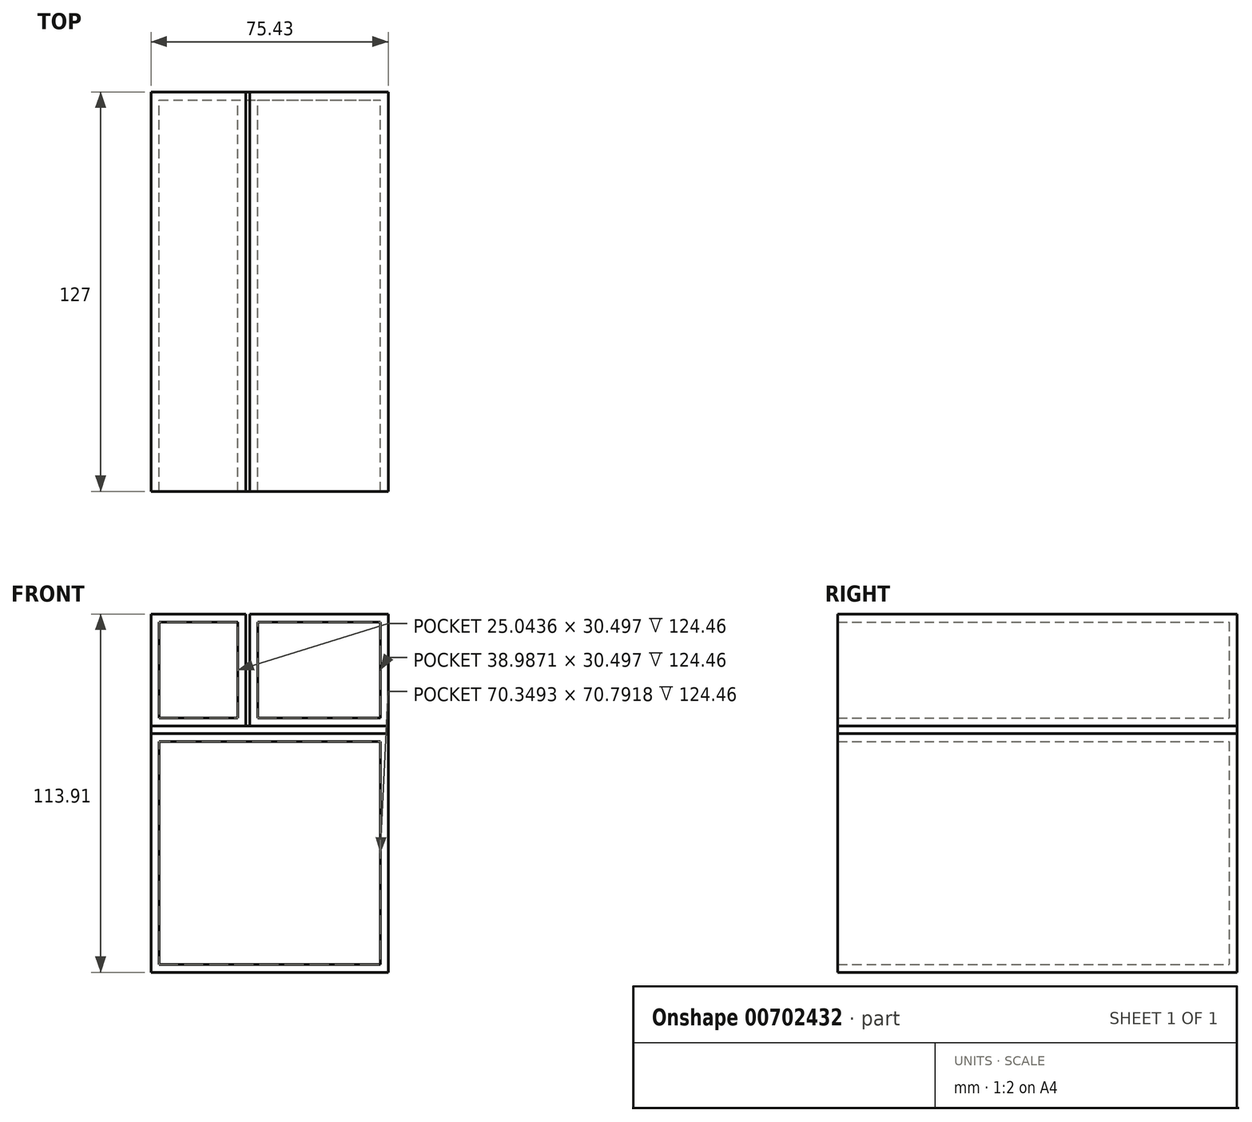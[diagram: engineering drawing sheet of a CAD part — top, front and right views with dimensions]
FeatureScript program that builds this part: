
annotation { "Feature Type Name" : "Feature", "Feature Type Description" : "" }
export const myFeature = defineFeature(function(context is Context, id is Id, definition is map)
    precondition{}
    {
        {
            var Q0;
            Q0=qCreatedBy(makeId("Front.planeOp"),FACE);
            var sketch = newSketch(context, id + "F0", { "sketchPlane" : qUnion([Q0])});
            skLineSegment(sketch, "E0.bottom", {"start": v(-89.02, 35.58) * mm, "end": v(-13.59, 35.58) * mm});
            skLineSegment(sketch, "E0.top", {"start": v(-89.02, -78.33) * mm, "end": v(-13.59, -78.33) * mm});
            skLineSegment(sketch, "E0.left", {"start": v(-89.02, 35.58) * mm, "end": v(-89.02, -78.33) * mm});
            skLineSegment(sketch, "E0.right", {"start": v(-13.59, 35.58) * mm, "end": v(-13.59, -78.33) * mm});
            skLineSegment(sketch, "E1.bottom", {"start": v(-58.9, 35.58) * mm, "end": v(-57.66, 35.58) * mm});
            skLineSegment(sketch, "E1.top", {"start": v(-58.9, 0) * mm, "end": v(-57.66, 0) * mm});
            skLineSegment(sketch, "E1.left", {"start": v(-58.9, 35.58) * mm, "end": v(-58.9, 0) * mm});
            skLineSegment(sketch, "E1.right", {"start": v(-57.66, 35.58) * mm, "end": v(-57.66, 0) * mm});
            skLineSegment(sketch, "E2.bottom", {"start": v(-89.02, 0) * mm, "end": v(-13.59, 0) * mm});
            skLineSegment(sketch, "E2.top", {"start": v(-89.02, -2.46) * mm, "end": v(-13.59, -2.46) * mm});
            skLineSegment(sketch, "E2.left", {"start": v(-89.02, 0) * mm, "end": v(-89.02, -2.46) * mm});
            skLineSegment(sketch, "E2.right", {"start": v(-13.59, 0) * mm, "end": v(-13.59, -2.46) * mm});
            skSolve(sketch);
        }
        {
            var Q0;
            {var subQ3=sQuery(id+"F0.wireOp",EDGE,"E1.left");Q0=makeQuery(id+"F0.imprint","IMPRINT",FACE,{"disambiguationData":[TD([[makeQuery(id+"F0.imprint","IMPRINT",EDGE,{"derivedFrom":subQ3}),-1.0]])]});}
            var Q1;
            {var subQ5=sQuery(id+"F0.wireOp",EDGE,"E0.top");Q1=makeQuery(id+"F0.imprint","IMPRINT",FACE,{"disambiguationData":[TD([[makeQuery(id+"F0.imprint","IMPRINT",EDGE,{"derivedFrom":subQ5}),1.0]])]});}
            var Q2;
            {var subQ3=sQuery(id+"F0.wireOp",EDGE,"E1.right");Q2=makeQuery(id+"F0.imprint","IMPRINT",FACE,{"disambiguationData":[TD([[makeQuery(id+"F0.imprint","IMPRINT",EDGE,{"derivedFrom":subQ3}),1.0]])]});}
            extrude(context, id + "F1", {"entities" : qUnion([Q0, Q1, Q2]), "depth" : 127 * mm, "offsetDistance" : 25.4 * mm});
        }
        {
            var Q0;
            Q0=makeQuery(id+"F1.opExtrude","CAP_FACE",FACE,{"disambiguationData":[OSD([sQuery(id+"F0.wireOp",EDGE,"E0.bottom"),sQuery(id+"F0.wireOp",EDGE,"E0.top"),sQuery(id+"F0.wireOp",EDGE,"E0.left"),sQuery(id+"F0.wireOp",EDGE,"E0.right"),sQuery(id+"F0.wireOp",EDGE,"E1.left"),sQuery(id+"F0.wireOp",EDGE,"E1.right"),sQuery(id+"F0.wireOp",EDGE,"6tspboNq-iTF7-SEg3-7sIw-ZveFWh7bHf5g")])],"isStart":false});
            shell(context, id + "F2", {"entities" : qUnion([Q0]), "thickness" : 2.54 * mm});
        }
        {
            var Q0;
            Q0=makeQuery(id+"F0.imprint","IMPRINT",FACE,{"disambiguationData":[TD([[makeQuery(id+"F0.imprint","IMPRINT",EDGE,{"derivedFrom":sQuery(id+"F0.wireOp",EDGE,"E2.top")}),1.0]])]});
            extrude(context, id + "F3", {"entities" : qUnion([Q0]), "depth" : 127 * mm, "offsetDistance" : 25.4 * mm});
        }
    });
